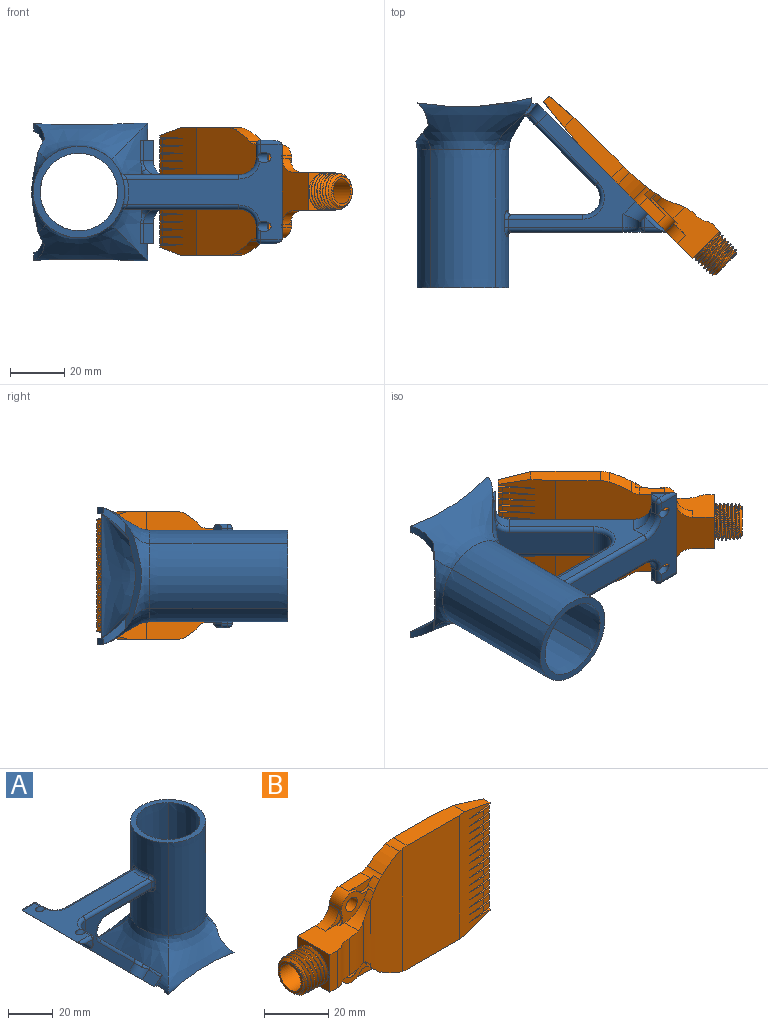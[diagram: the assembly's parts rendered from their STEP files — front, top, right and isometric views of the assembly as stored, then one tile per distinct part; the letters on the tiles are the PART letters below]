
ASSEMBLY  parts=2 mates=1
PART A: 89 faces, bbox 106.8x57.5x76.5 mm
  f0: bspline ~50.8x19.05mm, area 596mm2, adj f1,f9,f10,f11,f12,f13,f16,f17
  f1: extruded ~50.8x23.8mm, area 1219.5mm2, adj f0,f25,f26,f28,f69,f72,f73,f75
  f2: cylinder r=6.35mm len=10.84mm, axis (0,1,0), area 142.5mm2, adj f4,f9,f68,f81
  f3: plane 58.03x35.95mm, normal (0,0,1), area 742.6mm2, adj f8,f49,f50,f53,f59,f60,f63,f66
  f4: plane 26.35x9.53mm, normal (0,0,-1), area 246.9mm2, adj f2,f71,f77,f80
  f5: plane 4.11x4.03mm, normal (0,-1,0), area 8.4mm2, adj f38,f51,f52,f53
  f6: plane 4.11x2.9mm, normal (0,1,0), area 7mm2, adj f56,f57,f60,f61
  f7: plane 4.76x2.79mm, normal (0.71,0,-0.71), area 18.8mm2, adj f8,f42,f46,f57
  f8: plane 47.28x47.28mm, normal (-0.71,0,-0.71), area 1043.8mm2, adj f3,f7,f35,f37,f38,f39,f41,f42
  f9: plane 25.88x25.88mm, normal (0.71,0,0.71), area 352.2mm2, adj f0,f2,f62,f65,f82,f83
  f10: plane 5.77x5.3mm, normal (0,-1,0), area 6.4mm2, adj f0,f35,f36,f54,f88
  f11: plane 5.77x5.3mm, normal (0,1,0), area 6.4mm2, adj f0,f35,f40,f85,f88
  f12: cylinder r=100.06mm len=42.08mm, axis (0,-1,0), area 114.8mm2, adj f0,f16,f18,f29,f32,f34
  f13: cylinder r=100.06mm len=42.08mm, axis (0,-1,0), area 114.8mm2, adj f0,f17,f20,f31,f33,f34
  f14: bspline ~50.8x19.05mm, area 191.2mm2, adj f16,f17,f24,f30
  f15: offset ~55.88x24.13mm, area 198.2mm2, adj f18,f20,f22,f30
  f16: bspline ~50.8x19.05mm, area 719.6mm2, adj f0,f12,f14,f26,f29,f30
  f17: bspline ~50.8x19.05mm, area 719.6mm2, adj f0,f13,f14,f25,f30,f31
  f18: offset ~55.88x24.13mm, area 561.4mm2, adj f12,f15,f19,f23,f29,f30,f34
  f19: offset ~55.88x24.13mm, area 667.6mm2, adj f18,f20,f27,f34
  f20: offset ~55.88x24.13mm, area 561.4mm2, adj f13,f15,f19,f21,f30,f31,f34
  f21: extruded ~50.8x20.21mm, area 1140.1mm2, adj f20,f22,f27,f28
  f22: extruded ~50.8x20.21mm, area 1140.1mm2, adj f15,f21,f23,f28
  f23: extruded ~50.8x20.21mm, area 1140.1mm2, adj f18,f22,f27,f28
  f24: extruded ~50.8x23.8mm, area 1342.7mm2, adj f14,f25,f26,f28
  f25: extruded ~50.8x23.8mm, area 1342.7mm2, adj f1,f17,f24,f28
  f26: extruded ~50.8x23.8mm, area 1342.7mm2, adj f1,f16,f24,f28
  f27: extruded ~50.8x20.21mm, area 1140.1mm2, adj f19,f21,f23,f28
  f28: plane 33.67x33.67mm, normal (0,0,1), area 248.3mm2, adj f1,f21,f22,f23,f24,f25,f26,f27
  f29: cylinder r=12.7mm len=9.63mm, axis (0,-1,0), area 30.7mm2, adj f12,f16,f18,f30
  f30: plane 45.33x12.55mm, normal (0.79,0,-0.62), area 101.1mm2, adj f14,f15,f16,f17,f18,f20,f29,f31
  f31: cylinder r=12.7mm len=9.63mm, axis (0,-1,0), area 30.7mm2, adj f13,f17,f20,f30
  f32: plane 5.53x1.34mm, normal (0,1,0), area 3.3mm2, adj f0,f12,f34
  f33: plane 5.53x1.34mm, normal (0,-1,0), area 3.3mm2, adj f0,f13,f34
  f34: plane 46.32x5.95mm, normal (0,0,-1), area 120.5mm2, adj f0,f12,f13,f18,f19,f20,f32,f33
  f35: plane 38.1x1.8mm, normal (0,0,-1), area 68.4mm2, adj f8,f10,f11,f36,f40,f88
  f36: plane 7.62x3.86mm, normal (-0.71,0,0.71), area 39.8mm2, adj f10,f35,f43,f54
  f37: plane 46.95x42.11mm, normal (0,-1,0), area 422.8mm2, adj f8,f39,f43,f47,f65,f66,f68,f71
  f38: plane 7.02x3.46mm, normal (0.71,0,-0.71), area 23.7mm2, adj f5,f8,f39,f48,f51,f52
  f39: cylinder r=6.35mm len=9.15mm, axis (-0.71,0,-0.71), area 52.6mm2, adj f8,f37,f38,f47
  f40: plane 7.62x3.86mm, normal (-0.71,0,0.71), area 39.8mm2, adj f11,f35,f44,f85
  f41: plane 46.95x42.1mm, normal (0,1,0), area 423mm2, adj f8,f42,f44,f45,f74,f78,f80,f81
  f42: cylinder r=6.35mm len=9.14mm, axis (-0.71,0,-0.71), area 52.5mm2, adj f7,f8,f41,f45
  f43: cylinder r=5.08mm len=7.45mm, axis (-0.71,0,-0.71), area 39.2mm2, adj f8,f36,f37,f58,f62
  f44: cylinder r=5.08mm len=7.45mm, axis (-0.71,0,-0.71), area 39.2mm2, adj f8,f40,f41,f83,f84
  f45: cylinder r=6.35mm len=6.35mm, axis (0,0,1), area 36.6mm2, adj f41,f42,f46,f70
  f46: plane 4.76x2.36mm, normal (1,0,0), area 11.2mm2, adj f7,f45,f61,f67
  f47: cylinder r=6.35mm len=6.35mm, axis (0,0,1), area 36.6mm2, adj f37,f39,f48,f63
  f48: plane 4.76x2.36mm, normal (1,0,0), area 11.2mm2, adj f38,f47,f52,f59
  f49: cylinder r=1.9mm len=6.42mm, axis (-0.71,0,-0.71), area 48mm2, adj f3,f59,f63,f86
  f50: cylinder r=1.9mm len=6.42mm, axis (-0.71,0,-0.71), area 48mm2, adj f3,f67,f70,f87
  f51: cylinder r=1.59mm len=7.86mm, axis (-0.71,0,0.71), area 19mm2, adj f5,f8,f38,f53
  f52: cylinder r=1.59mm len=3.95mm, axis (0,0,-1), area 7.9mm2, adj f5,f38,f48,f55
  f53: cylinder r=1.59mm len=7.94mm, axis (1,0,0), area 15mm2, adj f3,f5,f51,f55
  f54: bspline ~7.68x1.46mm, area 9.7mm2, adj f0,f10,f36,f58
  f55: sphere r=1.59mm, area 4mm2, adj f52,f53,f59
  f56: cylinder r=1.59mm len=7.86mm, axis (0.71,0,-0.71), area 17mm2, adj f6,f8,f57,f60
  f57: cylinder r=1.59mm len=3.91mm, axis (0.71,0,0.71), area 7mm2, adj f6,f7,f56,f61
  f58: bspline ~4.27x2.12mm, area 5.4mm2, adj f0,f43,f54,f62
  f59: cylinder r=1.59mm len=4.76mm, axis (0,-1,0), area 10.9mm2, adj f3,f48,f49,f55,f63
  f60: cylinder r=1.59mm len=7.94mm, axis (-1,0,0), area 15mm2, adj f3,f6,f56,f64
  f61: cylinder r=1.59mm len=2.36mm, axis (0,0,-1), area 5.1mm2, adj f6,f46,f57,f64
  f62: torus R=6.67mm, axis (-0.71,0,-0.71), area 12.5mm2, adj f9,f43,f58,f65
  f63: torus R=7.94mm, axis (0,0,-1), area 26.2mm2, adj f3,f47,f49,f59,f66
  f64: sphere r=1.59mm, area 2.5mm2, adj f60,f61,f67
  f65: cylinder r=1.59mm len=23.13mm, axis (0.71,0,-0.71), area 77.6mm2, adj f9,f37,f62,f68
  f66: cylinder r=1.59mm len=42.3mm, axis (-1,0,0), area 104mm2, adj f3,f37,f63,f69
  f67: cylinder r=1.59mm len=4.76mm, axis (0,-1,0), area 10.9mm2, adj f3,f46,f50,f64,f70
  f68: torus R=7.94mm, axis (0,-1,0), area 40.7mm2, adj f2,f37,f65,f71
  f69: bspline ~3.83x3.55mm, area 7.5mm2, adj f1,f66,f72,f73
  f70: torus R=7.94mm, axis (0,0,-1), area 26.2mm2, adj f3,f45,f50,f67,f74
  f71: cylinder r=1.59mm len=27.51mm, axis (-1,0,0), area 67.1mm2, adj f4,f37,f68,f75
  f72: cylinder r=1.59mm len=3.18mm, axis (0,0,-1), area 5.7mm2, adj f1,f37,f69,f75
  f73: bspline ~12.56x2.65mm, area 22.7mm2, adj f1,f3,f69,f76
  f74: cylinder r=1.59mm len=42.3mm, axis (-1,0,0), area 104mm2, adj f3,f41,f70,f76
  f75: bspline ~3.83x3.27mm, area 7.5mm2, adj f1,f71,f72,f77
  f76: bspline ~3.35x3.27mm, area 7.5mm2, adj f1,f73,f74,f78
  f77: bspline ~12.56x2.65mm, area 22.7mm2, adj f1,f4,f75,f79
  f78: cylinder r=1.59mm len=3.18mm, axis (0,0,-1), area 5.7mm2, adj f1,f41,f76,f79
  f79: bspline ~3.83x3.55mm, area 7.5mm2, adj f1,f77,f78,f80
  f80: cylinder r=1.59mm len=27.51mm, axis (-1,0,0), area 67.1mm2, adj f4,f41,f79,f81
  f81: torus R=7.94mm, axis (0,1,0), area 40.7mm2, adj f2,f41,f80,f82
  f82: cylinder r=1.59mm len=23.13mm, axis (-0.71,0,0.71), area 77.6mm2, adj f9,f41,f81,f83
  f83: torus R=6.67mm, axis (-0.71,0,-0.71), area 12.5mm2, adj f9,f44,f82,f84
  f84: bspline ~4.27x2.12mm, area 5.4mm2, adj f0,f44,f83,f85
  f85: bspline ~7.68x1.46mm, area 9.7mm2, adj f0,f11,f40,f84
  f86: cone r=1.9mm half-angle=45deg, axis (-0.71,0,-0.71), area 16.2mm2, adj f8,f49
  f87: cone r=1.9mm half-angle=45deg, axis (-0.71,0,-0.71), area 16.2mm2, adj f8,f50
  f88: plane 38.19x0.61mm, normal (-0.71,0,-0.71), area 26.7mm2, adj f0,f10,f11,f35
PART B: 182 faces, bbox 90.7x14.7x47.5 mm
  f0: cone r=6.86mm half-angle=1.8deg, axis (1,0,0), area 54.5mm2, adj f2,f156,f178,f180,f181
  f1: cone r=6.57mm half-angle=45deg, axis (1,0,0), area 26.5mm2, adj f2,f177,f178,f179
  f2: cone r=6.57mm half-angle=45deg, axis (1,0,0), area 6.8mm2, adj f0,f1,f178,f180
  f3: plane 1x1mm, normal (1,0,0), area 0.8mm2, adj f17
  f4: plane 1x1mm, normal (1,0,0), area 0.8mm2, adj f18
  f5: plane 1x1mm, normal (1,0,0), area 0.8mm2, adj f19
  f6: plane 1x1mm, normal (1,0,0), area 0.8mm2, adj f20
  f7: plane 1x1mm, normal (1,0,0), area 0.8mm2, adj f21
  f8: plane 1x1mm, normal (1,0,0), area 0.8mm2, adj f22
  f9: plane 1x1mm, normal (1,0,0), area 0.8mm2, adj f23
  f10: plane 1x1mm, normal (1,0,0), area 0.8mm2, adj f24
  f11: plane 1x1mm, normal (1,0,0), area 0.8mm2, adj f25
  f12: plane 1x1mm, normal (1,0,0), area 0.8mm2, adj f26
  f13: plane 1x1mm, normal (1,0,0), area 0.8mm2, adj f27
  f14: plane 1x1mm, normal (1,0,0), area 0.8mm2, adj f28
  f15: plane 1x1mm, normal (1,0,0), area 0.8mm2, adj f29
  f16: plane 1x1mm, normal (1,0,0), area 0.8mm2, adj f30
  f17: cylinder r=0.5mm len=12mm, axis (-1,0,0), area 37.7mm2, adj f3,f34
  f18: cylinder r=0.5mm len=12mm, axis (-1,0,0), area 37.7mm2, adj f4,f34
  f19: cylinder r=0.5mm len=12mm, axis (-1,0,0), area 37.7mm2, adj f5,f34
  f20: cylinder r=0.5mm len=12mm, axis (-1,0,0), area 37.7mm2, adj f6,f34
  f21: cylinder r=0.5mm len=12mm, axis (-1,0,0), area 37.7mm2, adj f7,f34
  f22: cylinder r=0.5mm len=12mm, axis (-1,0,0), area 37.7mm2, adj f8,f34
  f23: cylinder r=0.5mm len=12mm, axis (-1,0,0), area 37.7mm2, adj f9,f34
  f24: cylinder r=0.5mm len=12mm, axis (-1,0,0), area 37.7mm2, adj f10,f34
  f25: cylinder r=0.5mm len=12mm, axis (-1,0,0), area 37.7mm2, adj f11,f34
  f26: cylinder r=0.5mm len=12mm, axis (-1,0,0), area 37.7mm2, adj f12,f34
  f27: cylinder r=0.5mm len=12mm, axis (-1,0,0), area 37.7mm2, adj f13,f34
  f28: cylinder r=0.5mm len=12mm, axis (-1,0,0), area 37.7mm2, adj f14,f34
  f29: cylinder r=0.5mm len=12mm, axis (-1,0,0), area 37.7mm2, adj f15,f34
  f30: cylinder r=0.5mm len=12mm, axis (-1,0,0), area 37.7mm2, adj f16,f34
  f31: cylinder r=8mm len=2.46mm, axis (0,1,0), area 2.5mm2, adj f32,f86,f87,f88
  f32: cylinder r=1.5mm len=1.5mm, axis (0,1,0), area 2.3mm2, adj f31,f86,f88,f157
  f33: cylinder r=3mm len=4.44mm, axis (0,1,0), area 6.7mm2, adj f79,f88,f89,f91,f92,f141
  f34: plane 41x2.98mm, normal (1,0,0), area 91.3mm2, adj f17,f18,f19,f20,f21,f22,f23,f24
  f35: plane 9.78x1.55mm, normal (0.08,-0.52,0.85), area 4.8mm2, adj f34,f36,f139
  f36: plane 9.78x1.55mm, normal (0.08,-0.52,-0.85), area 4.3mm2, adj f34,f35,f37,f139
  f37: plane 3.15x2.1mm, normal (0.16,-0.99,0), area 6.7mm2, adj f34,f36,f38,f139
  f38: plane 9.78x1.55mm, normal (0.08,-0.52,0.85), area 4.3mm2, adj f34,f37,f39,f139
  f39: plane 9.78x1.55mm, normal (0.08,-0.52,-0.85), area 4.3mm2, adj f34,f38,f40,f139
  f40: plane 3.15x2.1mm, normal (0.16,-0.99,0), area 6.7mm2, adj f34,f39,f41,f139
  f41: plane 9.78x1.55mm, normal (0.08,-0.52,0.85), area 4.3mm2, adj f34,f40,f42,f139
  f42: plane 9.78x1.55mm, normal (0.08,-0.52,-0.85), area 4.3mm2, adj f34,f41,f43,f139
  f43: plane 3.15x2.1mm, normal (0.16,-0.99,0), area 6.7mm2, adj f34,f42,f44,f139
  f44: plane 9.78x1.55mm, normal (0.08,-0.52,0.85), area 4.3mm2, adj f34,f43,f45,f139
  f45: plane 9.78x1.55mm, normal (0.08,-0.52,-0.85), area 4.3mm2, adj f34,f44,f46,f139
  f46: plane 3.15x2.1mm, normal (0.16,-0.99,0), area 6.7mm2, adj f34,f45,f47,f139
  f47: plane 9.78x1.55mm, normal (0.08,-0.52,0.85), area 4.3mm2, adj f34,f46,f48,f139
  f48: plane 9.78x1.55mm, normal (0.08,-0.52,-0.85), area 4.3mm2, adj f34,f47,f49,f139
  f49: plane 3.15x2.1mm, normal (0.16,-0.99,0), area 6.7mm2, adj f34,f48,f50,f139
  f50: plane 9.78x1.55mm, normal (0.08,-0.52,0.85), area 4.3mm2, adj f34,f49,f51,f139
  f51: plane 9.78x1.55mm, normal (0.08,-0.52,-0.85), area 4.3mm2, adj f34,f50,f52,f139
  f52: plane 3.15x2.1mm, normal (0.16,-0.99,0), area 6.7mm2, adj f34,f51,f53,f139
  f53: plane 9.78x1.55mm, normal (0.08,-0.52,0.85), area 4.3mm2, adj f34,f52,f54,f139
  f54: plane 9.78x1.55mm, normal (0.08,-0.52,-0.85), area 4.3mm2, adj f34,f53,f55,f139
  f55: plane 3.15x2.1mm, normal (0.16,-0.99,0), area 6.7mm2, adj f34,f54,f56,f139
  f56: plane 9.78x1.55mm, normal (0.08,-0.52,0.85), area 4.3mm2, adj f34,f55,f57,f139
  f57: plane 9.78x1.55mm, normal (0.08,-0.52,-0.85), area 4.3mm2, adj f34,f56,f58,f139
  f58: plane 3.15x2.1mm, normal (0.16,-0.99,0), area 6.7mm2, adj f34,f57,f59,f139
  f59: plane 9.78x1.55mm, normal (0.08,-0.52,0.85), area 4.3mm2, adj f34,f58,f60,f139
  f60: plane 9.78x1.55mm, normal (0.08,-0.52,-0.85), area 4.3mm2, adj f34,f59,f61,f139
  f61: plane 3.15x2.1mm, normal (0.16,-0.99,0), area 6.7mm2, adj f34,f60,f62,f139
  f62: plane 9.78x1.55mm, normal (0.08,-0.52,0.85), area 4.3mm2, adj f34,f61,f63,f139
  f63: plane 9.78x1.55mm, normal (0.08,-0.52,-0.85), area 4.3mm2, adj f34,f62,f64,f139
  f64: plane 3.15x2.1mm, normal (0.16,-0.99,0), area 6.7mm2, adj f34,f63,f65,f139
  f65: plane 9.78x1.55mm, normal (0.08,-0.52,0.85), area 4.3mm2, adj f34,f64,f66,f139
  f66: plane 9.78x1.55mm, normal (0.08,-0.52,-0.85), area 4.3mm2, adj f34,f65,f67,f139
  f67: plane 3.15x2.1mm, normal (0.16,-0.99,0), area 6.7mm2, adj f34,f66,f68,f139
  f68: plane 9.78x1.55mm, normal (0.08,-0.52,0.85), area 4.3mm2, adj f34,f67,f69,f139
  f69: plane 9.78x1.55mm, normal (0.08,-0.52,-0.85), area 4.3mm2, adj f34,f68,f70,f139
  f70: plane 3.15x2.1mm, normal (0.16,-0.99,0), area 6.7mm2, adj f34,f69,f71,f139
  f71: plane 9.78x1.55mm, normal (0.08,-0.52,0.85), area 4.3mm2, adj f34,f70,f72,f139
  f72: plane 9.78x1.55mm, normal (0.08,-0.52,-0.85), area 4.3mm2, adj f34,f71,f73,f139
  f73: plane 3.15x2.1mm, normal (0.16,-0.99,0), area 6.7mm2, adj f34,f72,f74,f139
  f74: plane 9.78x1.55mm, normal (0.08,-0.52,0.85), area 4.3mm2, adj f34,f73,f75,f139
  f75: plane 9.78x1.55mm, normal (0.08,-0.52,-0.85), area 4.3mm2, adj f34,f74,f76,f139
  f76: plane 3.15x2.1mm, normal (0.16,-0.99,0), area 6.7mm2, adj f34,f75,f77,f139
  f77: plane 9.78x1.55mm, normal (0.08,-0.52,0.85), area 4.3mm2, adj f34,f76,f78,f139
  f78: plane 9.78x1.55mm, normal (0.08,-0.52,-0.85), area 4.8mm2, adj f34,f77,f139
  f79: cylinder r=28mm len=2.96mm, axis (0,1,0), area 9.4mm2, adj f33,f84,f85,f88,f141
  f80: cylinder r=3mm len=4.44mm, axis (0,1,0), area 6.7mm2, adj f83,f141,f142,f143,f144,f148
  f81: cylinder r=1.5mm len=1.5mm, axis (0,1,0), area 2.3mm2, adj f82,f147,f148,f173
  f82: cylinder r=8mm len=2.45mm, axis (0,1,0), area 2.5mm2, adj f81,f146,f147,f148
  f83: cylinder r=28mm len=2.96mm, axis (0,1,0), area 9.4mm2, adj f80,f84,f141,f148,f149
  f84: cylinder r=15mm len=24.94mm, axis (0,0,-1), area 103.4mm2, adj f79,f83,f85,f141,f149,f150
  f85: cylinder r=10mm len=8.47mm, axis (0,1,0), area 42.7mm2, adj f79,f84,f88,f150,f157
  f86: plane 6.53x4.91mm, normal (0,-1,0), area 8.9mm2, adj f31,f32,f87,f157,f158
  f87: cylinder r=4.66mm len=1mm, axis (0,1,0), area 1mm2, adj f31,f86,f88,f158
  f88: plane 13x9.9mm, normal (0,-1,0), area 57mm2, adj f31,f32,f33,f79,f85,f87,f89,f90
  f89: plane 1x0.34mm, normal (0.74,0,0.68), area 0.5mm2, adj f33,f88,f91,f159
  f90: plane 5.2x0.97mm, normal (-0.99,0,0.15), area 5.1mm2, adj f88,f158,f159,f174
  f91: plane 10.75x3.43mm, normal (0,-1,0), area 16.8mm2, adj f33,f89,f92,f159,f160,f161
  f92: cylinder r=27mm len=3.24mm, axis (0,1,0), area 10.5mm2, adj f33,f91,f141,f161
  f93: plane 13.36x1.88mm, normal (0.07,0.52,-0.85), area 5mm2, adj f34,f94,f137,f165
  f94: plane 13.36x1.88mm, normal (0.07,0.52,0.85), area 5.1mm2, adj f34,f93,f165
  f95: plane 12x4.96mm, normal (0.24,0,0.97), area 49.1mm2, adj f34,f139,f164,f165
  f96: plane 13.36x1.88mm, normal (0.07,0.52,-0.85), area 5.1mm2, adj f34,f97,f165
  f97: plane 13.36x1.88mm, normal (0.07,0.52,0.85), area 5mm2, adj f34,f96,f98,f165
  f98: plane 2.1x1.66mm, normal (0.14,0.99,0), area 3.5mm2, adj f34,f97,f99,f165
  f99: plane 13.36x1.88mm, normal (0.07,0.52,-0.85), area 5mm2, adj f34,f98,f100,f165
  f100: plane 13.36x1.88mm, normal (0.07,0.52,0.85), area 5mm2, adj f34,f99,f101,f165
  f101: plane 2.1x1.66mm, normal (0.14,0.99,0), area 3.5mm2, adj f34,f100,f102,f165
  f102: plane 13.36x1.88mm, normal (0.07,0.52,-0.85), area 5mm2, adj f34,f101,f103,f165
  f103: plane 13.36x1.88mm, normal (0.07,0.52,0.85), area 5mm2, adj f34,f102,f104,f165
  f104: plane 2.1x1.66mm, normal (0.14,0.99,0), area 3.5mm2, adj f34,f103,f105,f165
  f105: plane 13.36x1.88mm, normal (0.07,0.52,-0.85), area 5mm2, adj f34,f104,f106,f165
  f106: plane 13.36x1.88mm, normal (0.07,0.52,0.85), area 5mm2, adj f34,f105,f107,f165
  f107: plane 2.1x1.66mm, normal (0.14,0.99,0), area 3.5mm2, adj f34,f106,f108,f165
  f108: plane 13.36x1.88mm, normal (0.07,0.52,-0.85), area 5mm2, adj f34,f107,f109,f165
  f109: plane 13.36x1.88mm, normal (0.07,0.52,0.85), area 5mm2, adj f34,f108,f110,f165
  f110: plane 2.1x1.66mm, normal (0.14,0.99,0), area 3.5mm2, adj f34,f109,f111,f165
  f111: plane 13.36x1.88mm, normal (0.07,0.52,-0.85), area 5mm2, adj f34,f110,f112,f165
  f112: plane 13.36x1.88mm, normal (0.07,0.52,0.85), area 5mm2, adj f34,f111,f113,f165
  f113: plane 2.1x1.66mm, normal (0.14,0.99,0), area 3.5mm2, adj f34,f112,f114,f165
  f114: plane 13.36x1.88mm, normal (0.07,0.52,-0.85), area 5mm2, adj f34,f113,f115,f165
  f115: plane 13.36x1.88mm, normal (0.07,0.52,0.85), area 5mm2, adj f34,f114,f116,f165
  f116: plane 2.1x1.66mm, normal (0.14,0.99,0), area 3.5mm2, adj f34,f115,f117,f165
  f117: plane 13.36x1.88mm, normal (0.07,0.52,-0.85), area 5mm2, adj f34,f116,f118,f165
  f118: plane 13.36x1.88mm, normal (0.07,0.52,0.85), area 5mm2, adj f34,f117,f119,f165
  f119: plane 2.1x1.66mm, normal (0.14,0.99,0), area 3.5mm2, adj f34,f118,f120,f165
  f120: plane 13.36x1.88mm, normal (0.07,0.52,-0.85), area 5mm2, adj f34,f119,f121,f165
  f121: plane 13.36x1.88mm, normal (0.07,0.52,0.85), area 5mm2, adj f34,f120,f122,f165
  f122: plane 2.1x1.66mm, normal (0.14,0.99,0), area 3.5mm2, adj f34,f121,f123,f165
  f123: plane 13.36x1.88mm, normal (0.07,0.52,-0.85), area 5mm2, adj f34,f122,f124,f165
  f124: plane 13.36x1.88mm, normal (0.07,0.52,0.85), area 5mm2, adj f34,f123,f125,f165
  f125: plane 2.1x1.66mm, normal (0.14,0.99,0), area 3.5mm2, adj f34,f124,f126,f165
  f126: plane 13.36x1.88mm, normal (0.07,0.52,-0.85), area 5mm2, adj f34,f125,f127,f165
  f127: plane 13.36x1.88mm, normal (0.07,0.52,0.85), area 5mm2, adj f34,f126,f128,f165
  f128: plane 2.1x1.66mm, normal (0.14,0.99,0), area 3.5mm2, adj f34,f127,f129,f165
  f129: plane 13.36x1.88mm, normal (0.07,0.52,-0.85), area 5mm2, adj f34,f128,f130,f165
  f130: plane 13.36x1.88mm, normal (0.07,0.52,0.85), area 5mm2, adj f34,f129,f131,f165
  f131: plane 2.1x1.66mm, normal (0.14,0.99,0), area 3.5mm2, adj f34,f130,f132,f165
  f132: plane 13.36x1.88mm, normal (0.07,0.52,-0.85), area 5mm2, adj f34,f131,f133,f165
  f133: plane 13.36x1.88mm, normal (0.07,0.52,0.85), area 5mm2, adj f34,f132,f134,f165
  f134: plane 2.1x1.66mm, normal (0.14,0.99,0), area 3.5mm2, adj f34,f133,f135,f165
  f135: plane 13.36x1.88mm, normal (0.07,0.52,-0.85), area 5mm2, adj f34,f134,f136,f165
  f136: plane 13.36x1.88mm, normal (0.07,0.52,0.85), area 5mm2, adj f34,f135,f137,f165
  f137: plane 2.1x1.66mm, normal (0.14,0.99,0), area 3.5mm2, adj f34,f93,f136,f165
  f138: plane 12x4.96mm, normal (0.24,0,-0.97), area 49.1mm2, adj f34,f139,f165,f166
  f139: plane 47x14.6mm, normal (0.07,-1,0), area 490.5mm2, adj f34,f35,f36,f37,f38,f39,f40,f41
  f140: plane 47x24.9mm, normal (0,-1,0), area 1170mm2, adj f139,f141,f163,f164,f166,f167
  f141: cylinder r=83mm len=46.57mm, axis (0,0,-1), area 601.4mm2, adj f33,f79,f80,f83,f84,f92,f140,f142
  f142: cylinder r=27mm len=3.24mm, axis (0,1,0), area 10.5mm2, adj f80,f141,f143,f169
  f143: plane 10.75x3.43mm, normal (0,-1,0), area 16.8mm2, adj f80,f142,f144,f169,f170,f171
  f144: plane 1x0.34mm, normal (0.74,0,-0.68), area 0.5mm2, adj f80,f143,f148,f171
  f145: plane 5.2x0.97mm, normal (-0.99,0,-0.15), area 5.1mm2, adj f148,f171,f172,f174
  f146: cylinder r=4.67mm len=1mm, axis (0,1,0), area 1mm2, adj f82,f147,f148,f172
  f147: plane 6.53x4.88mm, normal (0,-1,0), area 8.9mm2, adj f81,f82,f146,f172,f173
  f148: plane 13x9.9mm, normal (0,-1,0), area 57mm2, adj f80,f81,f82,f83,f144,f145,f146,f149
  f149: cylinder r=10mm len=8.47mm, axis (0,1,0), area 42.7mm2, adj f83,f84,f148,f150,f173
  f150: cylinder r=17.5mm len=15.72mm, axis (0,0,-1), area 132.3mm2, adj f84,f85,f149,f151,f157,f173
  f151: cylinder r=7mm len=14.2mm, axis (0,0,-1), area 64.1mm2, adj f150,f152,f157,f173
  f152: cylinder r=5mm len=14.2mm, axis (0,0,-1), area 46.3mm2, adj f151,f153,f157,f173
  f153: plane 14.2x3.25mm, normal (0,-1,0), area 46.1mm2, adj f152,f156,f157,f173
  f154: cylinder r=2.5mm len=5.2mm, axis (0,-1,0), area 81.7mm2, adj f148,f174
  f155: cylinder r=2.5mm len=5.2mm, axis (0,-1,0), area 81.7mm2, adj f88,f174
  f156: plane 14.73x14.73mm, normal (-1,0,0), area 72mm2, adj f0,f153,f157,f173,f174,f178,f179,f180
  f157: plane 15.39x14.2mm, normal (0,0,1), area 165mm2, adj f32,f85,f86,f88,f150,f151,f152,f153
  f158: cylinder r=6mm len=5.93mm, axis (0,1,0), area 36mm2, adj f86,f87,f88,f90,f157,f174
  f159: cylinder r=4.5mm len=7.76mm, axis (0,1,0), area 36.1mm2, adj f88,f89,f90,f91,f160,f174
  f160: plane 9.41x4.2mm, normal (-0.05,0,1), area 39.5mm2, adj f91,f159,f161,f174
  f161: cylinder r=5mm len=7mm, axis (0,1,0), area 17.3mm2, adj f91,f92,f141,f160,f162,f174
  f162: cylinder r=30mm len=8.16mm, axis (0,1,0), area 59.9mm2, adj f141,f161,f163,f174
  f163: cylinder r=10mm len=6.04mm, axis (0,1,0), area 20.7mm2, adj f140,f141,f162,f164,f174
  f164: plane 25.44x6mm, normal (0,0,1), area 148.5mm2, adj f95,f139,f140,f163,f165,f174
  f165: plane 47x21.2mm, normal (0.09,1,0), area 836.1mm2, adj f34,f93,f94,f95,f96,f97,f98,f99
  f166: plane 25.44x6mm, normal (0,0,-1), area 148.5mm2, adj f138,f139,f140,f165,f167,f174
  f167: cylinder r=10mm len=6.04mm, axis (0,1,0), area 20.7mm2, adj f140,f141,f166,f168,f174
  f168: cylinder r=30mm len=8.16mm, axis (0,1,0), area 59.9mm2, adj f141,f167,f169,f174
  f169: cylinder r=5mm len=7mm, axis (0,1,0), area 17.3mm2, adj f141,f142,f143,f168,f170,f174
  f170: plane 9.41x4.2mm, normal (-0.05,0,-1), area 39.5mm2, adj f143,f169,f171,f174
  f171: cylinder r=4.5mm len=7.76mm, axis (0,1,0), area 36.1mm2, adj f143,f144,f145,f148,f170,f174
  f172: cylinder r=6mm len=5.93mm, axis (0,1,0), area 36mm2, adj f145,f146,f147,f148,f173,f174
  f173: plane 15.39x14.2mm, normal (0,0,-1), area 165mm2, adj f81,f147,f148,f149,f150,f151,f152,f153
  f174: plane 58.3x47mm, normal (0,1,0), area 1999.5mm2, adj f90,f145,f154,f155,f156,f157,f158,f159
  f175: plane 9.25x9.25mm, normal (-1,0,0), area 67.1mm2, adj f176
  f176: cylinder r=4.62mm len=9.25mm, axis (1,0,0), area 259.5mm2, adj f175,f177
  f177: plane 10.96x10.96mm, normal (-1,0,0), area 27.3mm2, adj f1,f176
  f178: bspline ~13.9x13.85mm, area 270.4mm2, adj f0,f1,f2,f156,f179
  f179: bspline ~12.01x12mm, area 45.8mm2, adj f1,f156,f178,f180
  f180: bspline ~13.88x13.78mm, area 282.3mm2, adj f0,f2,f156,f179,f181
  f181: bspline ~6.89x3.74mm, area 0mm2, adj f0,f156,f180
PLACE A rot(axis=(0,-0.71,0.71),180deg) t=(-235.67,30.06,45.86)mm
PLACE B rot(axis=(0,0,1),135deg) t=(-113.32,-31.45,20.66)mm
MATE fastened B.f87 <-> A.f49  axis (-0.71,-0.71,0) through (-138.85,-15.96,33.16)mm
